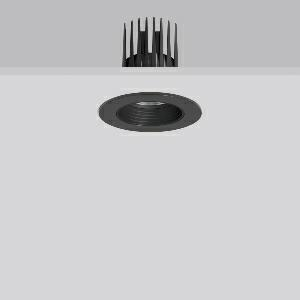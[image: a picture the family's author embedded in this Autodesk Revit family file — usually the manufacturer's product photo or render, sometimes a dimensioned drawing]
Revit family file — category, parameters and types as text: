
# Revit family: heledon_mini_e_901747_003_3_76_1344
name_source: partatom
category: Lighting Fixtures
units: mm (PartAtom-declared; Revit-internal decimal feet)

## family parameters
Cut with Voids When Loaded = No
Host = Face
Light Source = No
Part Type = Normal
Room Calculation Point = No
Round Connector Dimension = Use Diameter
Shared = No

## types (1)
- HELEDON mini E (1 x LED Modul 935, 1950 lm, 3500)
    Apparent Load = 20 VA
    Approval mark = CE
    CIE Flux Codes = 95 100 100 100 100
    Color Rendering = 92
    Color Temperature = 3500
    Default Elevation = 1800 mm
    Description = Series: HELEDON mini
Round recessed downlight. Housing: die-cast aluminium, powder-coated. Black plastic ring and recessed LED to prevent glare from the side. Optical assembly with lens made of plastic (polycarbonate) for the best homogeneous light distribution - can be changed without tools. Best colour rendering index Ra>90. Suitable for Recessed ceiling mounting. Installation without tools thanks to spring fastening system. Including separate LED converter with connecting cable 600 mm.High quality converter without flickering and stroboscopic effect. Through-wiring box (5 pole) available as accessory. The following accessories can be mounted without use of tools: interchangeable lenses, decorative glasses, honeycomb louvre, clear and frosted diffusers, white interchangeable plastic ring. 
Colour: deep black, matt (RAL 9005)
Diameter: 124 mm
Height: 3 mm
Cut-out diameter: 114 mm
Recess height: 170 mm
Luminaire: recess height: 120 mm
Lamp: LED
Socket: without socket
Colour temperature: 3500K
Colour rendering index (CRI): 92
System power: 20 W
Rated luminous flux: 1950 lm
Luminous efficiency: 98 lm/W
Control gear: Converter, dimmable, DALI
Protection class: II
Type of protection: IP 20
    Height = 0 mm  [stored 0 ft]
    Lamp = 1 x LED Modul 935
    Lamp Light Flux = 1950 lm
    Lamp count = 1
    Length = 124 mm  [stored 0.406824 ft]
    Lifetime = 50000 h
    Luminous efficacy = 98 lm/W
    Manufacturer = RZB
    ModVariant = No
    Model = 901747.003.3.76
    Mounting Place = Ceiling
    Mounting Type = Recessed
    Number of Poles = 1
    OnlyDefault = Yes
    Power Factor = 1
    Product Name = HELEDON mini E
    Product group = Recessed downlights
    ProductGroupID = 402
    Protection Class = Protection class II
    Protection Degree = IP 20
    RLX_Detail_Level = 1
    RLX_Emergency_Light_Flux = 0 lm
    RLX_Emergency_Type = 0
    RLX_Emergency_Type_DB = No
    RlxData = <blob elided: 134101 chars, md5=1f3fe19a>
    Socket = socket
    Standby Power = 0 W
    System Light Flux = 1950 lm
    System Power = 20 W
    Type Comments = Product without accessories
    Type Image = 901656.003.jpg
    URL = http://relux.com
    VarID = ---
    Voltage = 230 V
    Voltage Range = 220-240 V
    Weight = 0.00 kg
    Width = 0 mm  [stored 0 ft]

note: [stored X ft] marks values corroborated as IEEE doubles in the binary element streams (Revit-internal decimal feet)

## geometry (parser evidence)
native form markers: Blend x4, Sweep x9
no freeform markers — native parametric forms only
